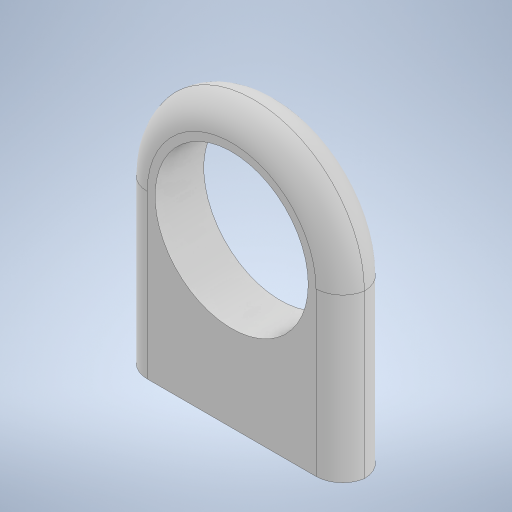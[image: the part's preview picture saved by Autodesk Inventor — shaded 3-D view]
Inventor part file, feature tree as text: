
AUTODESK INVENTOR PART (.ipt)
format: ipt  version: 2024 (Build 280153000, 153)  size: 329,216 bytes
history: native  units: in
note: dims shown in document units (in); Inventor stores cm internally (conversion verified against a paired STEP export)
features: extrude x7, sketch x7, projected_geometry x3, plane x1, fillet x1
ambient origin geometry x8: Origin, YZ Plane, XZ Plane, XY Plane, X Axis, Y Axis, Z Axis, Center Point
bodies: Solid1 (feature_tree)
feature tree (19):
  extrude  "Extrusion1"  Depth=1.25in
  extrude  "Extrusion2"  Depth=0.2756in TaperAngle=0.0deg
  extrude  "Extrusion3"  Depth=0.4921in
  plane  "Work Plane1"
  extrude  "Extrusion7"  Depth=0.1083in TaperAngle=0.0deg
  extrude  "Extrusion8"  Depth=0.2756in TaperAngle=0.0deg
  sketch  "Sketch9"  dims[d34=1.0in d35=1.0in d36=0.0in d37=0.0in d38=0.0in]
  extrude  "Extrusion9"  Depth=1.0in TaperAngle=0.0deg
  fillet  "Fillet6"  [1 undecoded]
  extrude  "Extrusion10"  Depth=0.15in
  sketch  "Sketch1"  dims[d0=0.8661in d1=1.25in]
  sketch  "Sketch3"  dims[d2=1.125in d3=0.2756in d4=0.0in]
  sketch  "Sketch4"  dims[d5=0.4921in d6=0.4921in]
  projected_geometry  "Projected Loop1"
  sketch  "Sketch7"  dims[d7=1.8898in d8=0.1083in d9=0.0in]
  projected_geometry  "Projected Loop2"
  sketch  "Sketch8"  dims[d10=0.9843in d11=0.2756in d12=0.0in]
  sketch  "Sketch10"  dims[d39=0.275in d40=0.275in d41=0.1181in d42=0.1181in d43=0.5in d44=0.0in d45=0.15in d46=0.0984in d47=0.0in]
  projected_geometry  "Projected Loop3"
note: 1 required parameter value undecoded (feature->parameter linkage not recoverable at this tier; creation-order binding heuristic only, values carry confidence <= 0.55)
